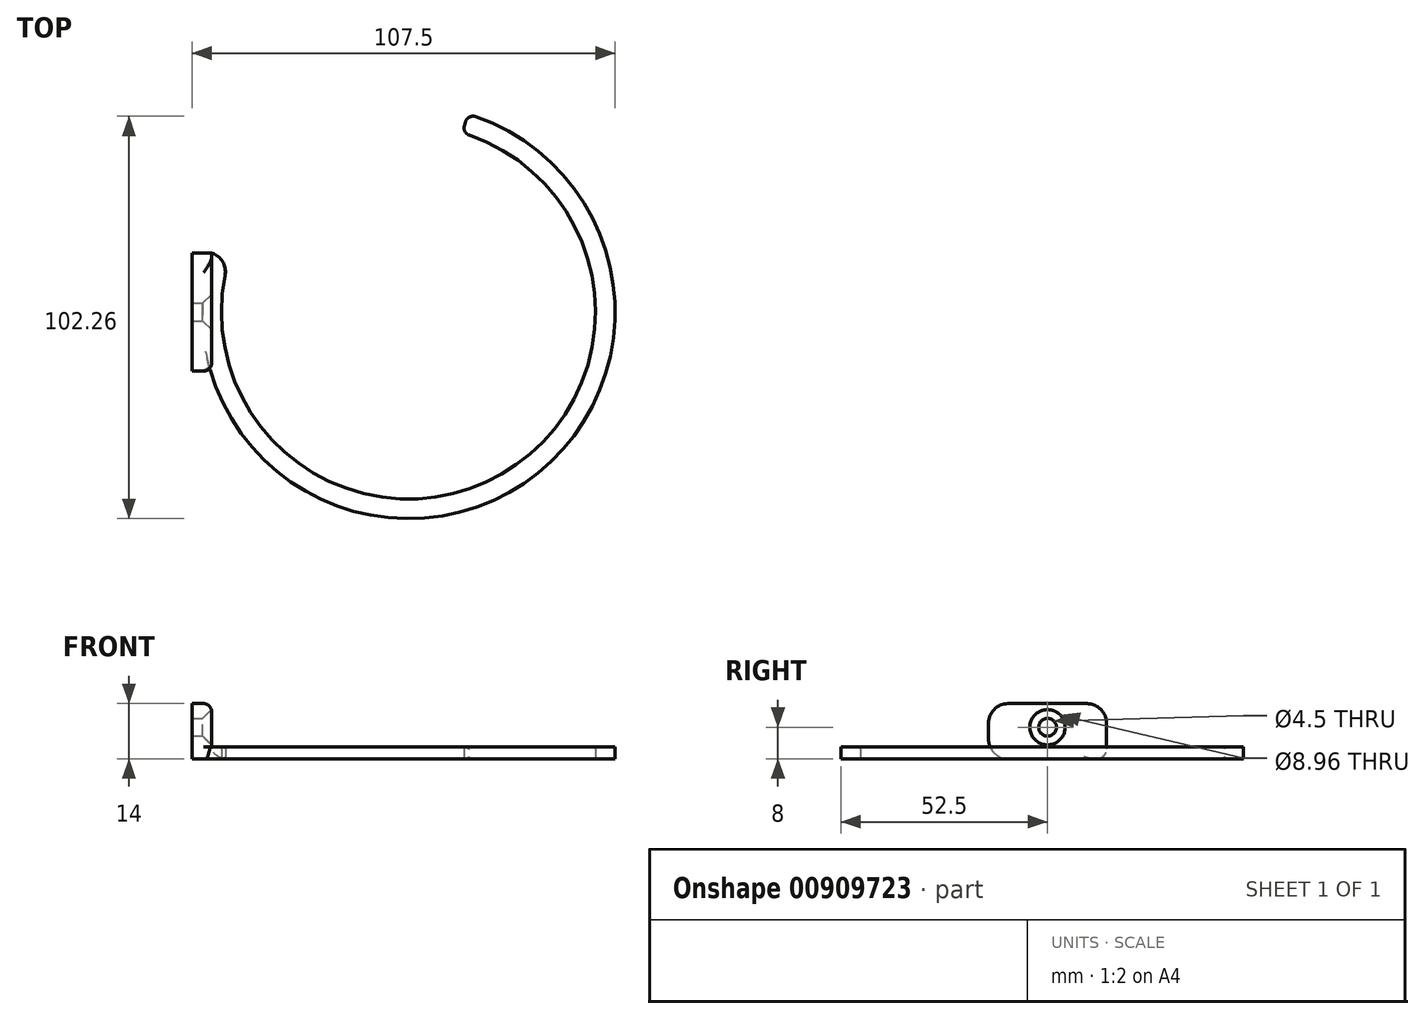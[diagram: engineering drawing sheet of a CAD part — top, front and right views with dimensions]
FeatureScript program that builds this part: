
annotation { "Feature Type Name" : "Feature", "Feature Type Description" : "" }
export const myFeature = defineFeature(function(context is Context, id is Id, definition is map)
    precondition{}
    {
        {
            var Q0;
            Q0=qCreatedBy(makeId("Right.planeOp"),FACE);
            var sketch = newSketch(context, id + "F0", { "sketchPlane" : qUnion([Q0])});
            skArc(sketch, "E0", {"start": v(15.09, 50.29) * mm, "mid": v(15.04, 50.3) * mm, "end": v(15, 50.31) * mm});
            skArc(sketch, "E1", {"start": v(9.25, 46.59) * mm, "mid": v(-40.7, -24.49) * mm, "end": v(45.5, -13.65) * mm});
            skLineSegment(sketch, "E2.bottom", {"start": v(15, 50) * mm, "end": v(-15, 50) * mm});
            skLineSegment(sketch, "E2.top", {"start": v(15, 55) * mm, "end": v(-15, 55) * mm});
            skLineSegment(sketch, "E2.left", {"start": v(15, 50) * mm, "end": v(15, 55) * mm});
            skLineSegment(sketch, "E2.right", {"start": v(-15, 50) * mm, "end": v(-15, 55) * mm});
            skPoint(sketch, "E2.middle", {"position": v(0, 52.5) * mm});
            skLineSegment(sketch, "E3", {"start": v(15.02, 50.06) * mm, "end": v(35.4, 118.02) * mm});
            skLineSegment(sketch, "E4", {"start": v(45.5, -13.65) * mm, "end": v(50.29, -15.09) * mm});
            skArc(sketch, "E5.trimOffspring", {"start": v(-15, 50.31) * mm, "mid": v(-37.15, -37.1) * mm, "end": v(50.29, -15.09) * mm});
            skPoint(sketch, "E6.visualSharp", {"position": v(13.65, 45.5) * mm});
            skArc(sketch, "E6.filletArc", {"start": v(9.25, 46.59) * mm, "mid": v(12.8, 47.2) * mm, "end": v(15.02, 50.06) * mm});
            skSolve(sketch);
        }
        {
            var Q0;
            {var subQ6=sQuery(id+"F0.wireOp",EDGE,"E1");Q0=makeQuery(id+"F0.imprint","IMPRINT",FACE,{"disambiguationData":[TD([[makeQuery(id+"F0.imprint","IMPRINT",EDGE,{"derivedFrom":subQ6}),-1.0]])]});}
            extrude(context, id + "F1", {"entities" : qUnion([Q0]), "depth" : 3 * mm, "offsetDistance" : 25 * mm});
        }
        {
            var Q0;
            {var subQ2=sQuery(id+"F0.wireOp",EDGE,"E2.top");Q0=makeQuery(id+"F0.imprint","IMPRINT",FACE,{"disambiguationData":[TD([[makeQuery(id+"F0.imprint","IMPRINT",EDGE,{"derivedFrom":subQ2}),1.0]])]});}
            extrude(context, id + "F2", {"entities" : qUnion([Q0]), "operationType" : NewBodyOperationType.ADD, "depth" : 14 * mm, "offsetDistance" : 25 * mm});
        }
        {
            var Q0;
            Q0=makeQuery(id+"F1.opExtrude","SWEPT_EDGE",EDGE,{"disambiguationData":[OSD([sQuery(id+"F0.wireOp",EDGE,"E4"),sQuery(id+"F0.wireOp",EDGE,"E5.trimOffspring")])]});
            var Q1;
            Q1=makeQuery(id+"F1.opExtrude","SWEPT_EDGE",EDGE,{"disambiguationData":[OSD([sQuery(id+"F0.wireOp",EDGE,"E1"),sQuery(id+"F0.wireOp",EDGE,"E4")])]});
            fillet(context, id + "F3", {"entities" : qUnion([Q0, Q1]), "radius" : 2 * mm, "tangentPropagation" : true, "allowEdgeOverflow" : false});
        }
        {
            var Q0;
            Q0=makeQuery(id+"F1.opExtrude","CAP_EDGE",EDGE,{"disambiguationData":[OSD([sQuery(id+"F0.wireOp",EDGE,"E1")])],"isStart":true});
            var Q1;
            Q1=makeQuery(id+"F1.opExtrude","CAP_EDGE",EDGE,{"disambiguationData":[OSD([sQuery(id+"F0.wireOp",EDGE,"E1")])],"isStart":false});
            var Q2;
            Q2=makeQuery(id+"F1.opExtrude","CAP_EDGE",EDGE,{"disambiguationData":[OSD([sQuery(id+"F0.wireOp",EDGE,"E6.filletArc")])],"isStart":false});
            fillet(context, id + "F4", {"entities" : qUnion([Q0, Q1, Q2]), "radius" : .5 * mm, "allowEdgeOverflow" : false});
        }
        {
            var Q0;
            Q0=makeQuery(id+"F2.opExtrude","CAP_EDGE",EDGE,{"disambiguationData":[OSD([sQuery(id+"F0.wireOp",EDGE,"E2.right")])],"isStart":false});
            var Q1;
            Q1=makeQuery(id+"F2.opExtrude","CAP_EDGE",EDGE,{"disambiguationData":[OSD([sQuery(id+"F0.wireOp",EDGE,"E2.left")])],"isStart":false});
            var Q2;
            Q2=makeQuery(id+"F2.opExtrude","CAP_EDGE",EDGE,{"disambiguationData":[OSD([sQuery(id+"F0.wireOp",EDGE,"E2.right")])],"isStart":true});
            fillet(context, id + "F5", {"entities" : qUnion([Q0, Q1, Q2]), "radius" : 5 * mm, "tangentPropagation" : true, "allowEdgeOverflow" : false});
        }
        {
            var Q0;
            Q0=makeQuery(id+"F2.opExtrude","CAP_EDGE",EDGE,{"disambiguationData":[OSD([sQuery(id+"F0.wireOp",EDGE,"E2.left")])],"isStart":true});
            fillet(context, id + "F6", {"entities" : qUnion([Q0]), "radius" : 2.5 * mm, "tangentPropagation" : true, "allowEdgeOverflow" : false});
        }
        {
            var Q0;
            Q0=makeQuery(id+"F2.opExtrude","CAP_EDGE",EDGE,{"disambiguationData":[OSD([sQuery(id+"F0.wireOp",EDGE,"E2.bottom")])],"isStart":false});
            var Q1;
            Q1=makeQuery(id+"F2.opExtrude","SWEPT_EDGE",EDGE,{"disambiguationData":[OSD([sQuery(id+"F0.wireOp",EDGE,"E2.bottom"),sQuery(id+"F0.wireOp",EDGE,"E2.right")])]});
            fillet(context, id + "F7", {"entities" : qUnion([Q0, Q1]), "radius" : 2 * mm, "allowEdgeOverflow" : false});
        }
        {
            var Q0;
            Q0=makeQuery(id+"F7.opFillet","SPLIT",FACE,{"disambiguationData":[OD(1.0)],"derivedFrom":makeQuery(id+"F2.opExtrude","SWEPT_FACE",FACE,{"disambiguationData":[OSD([sQuery(id+"F0.wireOp",EDGE,"E2.bottom")])]})});
            var sketch = newSketch(context, id + "F8", { "sketchPlane" : qUnion([Q0])});
            skPoint(sketch, "E7", {"position": v(8, 0) * mm});
            skSolve(sketch);
        }
        {
            var Q0;
            Q0=sQuery(id+"F8.wireOp",VERTEX,"E7");
            var Q1;
            Q1=makeQuery(id+"F1.opExtrude","SWEPT_BODY",BODY,{"disambiguationData":[OSD([sQuery(id+"F0.wireOp",EDGE,"E1"),sQuery(id+"F0.wireOp",EDGE,"E2.bottom"),sQuery(id+"F0.wireOp",EDGE,"E2.right"),sQuery(id+"F0.wireOp",EDGE,"E4"),sQuery(id+"F0.wireOp",EDGE,"E5.trimOffspring"),sQuery(id+"F0.wireOp",EDGE,"E6.filletArc")])]});
            hole(context, id + "F9", {"style" : HoleStyle.C_SINK, "endStyle" : HoleEndStyle.THROUGH, "standardTappedOrClearance" : lookupTablePath({ "standard" : "ISO", "fit" : "Normal", "size" : "M4", "type" : "Clearance" }), "standardBlindInLast" : lookupTablePath({ "fit" : "Normal", "standard" : "ISO", "engagement" : "75%", "pitch" : "0.7 mm", "size" : "M4", "type" : "Clearance & tapped" }), "holeDiameter" : 4.5 * mm, "cSinkDiameter" : 8.96 * mm, "cSinkAngle" : 90 * degree, "majorDiameter" : 5 * mm, "isTappedThrough" : true, "tappedDepth" : 12 * mm, "tapClearance" : 3, "locations" : qUnion([Q0]), "scope" : qUnion([Q1])});
        }
        {
            var Q0;
            Q0=makeQuery(id+"F1.opExtrude","SWEPT_BODY",BODY,{"disambiguationData":[OSD([sQuery(id+"F0.wireOp",EDGE,"E1"),sQuery(id+"F0.wireOp",EDGE,"E2.bottom"),sQuery(id+"F0.wireOp",EDGE,"E2.right"),sQuery(id+"F0.wireOp",EDGE,"E4"),sQuery(id+"F0.wireOp",EDGE,"E5.trimOffspring"),sQuery(id+"F0.wireOp",EDGE,"E6.filletArc")])]});
            var Q1;
            Q1=makeQuery(id+"F2.opExtrude","CAP_EDGE",EDGE,{"disambiguationData":[OSD([sQuery(id+"F0.wireOp",EDGE,"E2.top")])],"isStart":false});
            transform(context, id + "F10", {"entities" : qUnion([Q0]), "transformType" : TransformType.ROTATION, "transformAxis" : qUnion([Q1]), "angle" : 90 * degree, "makeCopy" : false});
        }
    });
